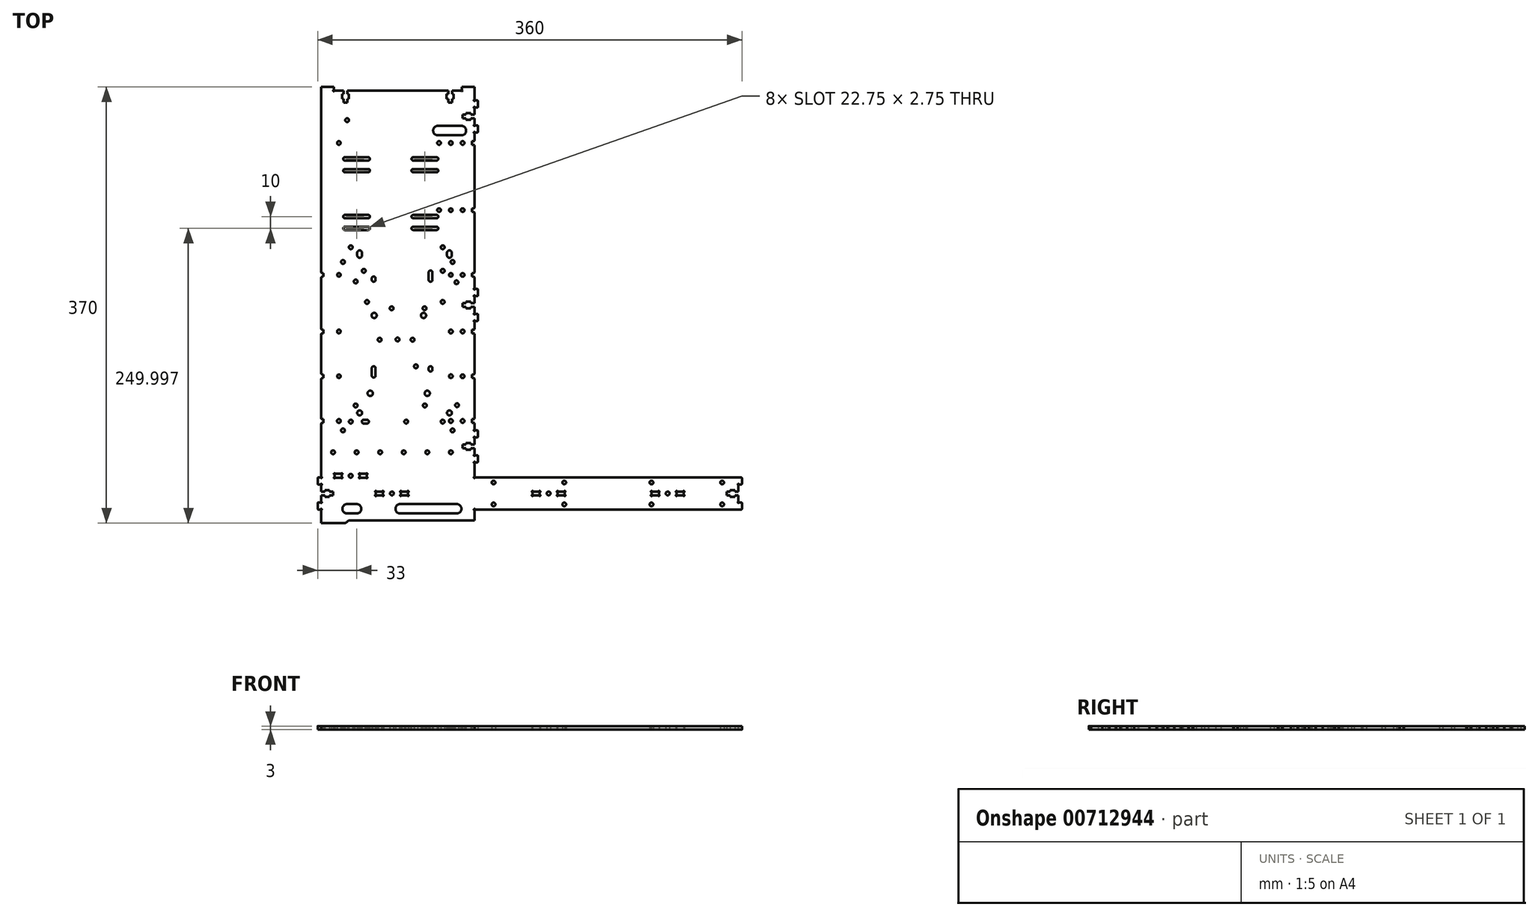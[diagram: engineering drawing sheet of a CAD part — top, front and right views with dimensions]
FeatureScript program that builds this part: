
annotation { "Feature Type Name" : "Feature", "Feature Type Description" : "" }
export const myFeature = defineFeature(function(context is Context, id is Id, definition is map)
    precondition{}
    {
        {
            var Q0;
            Q0=qCreatedBy(makeId("Top.planeOp"),FACE);
            var sketch = newSketch(context, id + "F0", { "sketchPlane" : qUnion([Q0])});
            skCircle(sketch, "E0", {"center": v(103.25, -146.86) * mm, "radius": 1.55 * mm});
            skCircle(sketch, "E1", {"center": v(-30.75, -146.86) * mm, "radius": 1.55 * mm});
            skCircle(sketch, "E2", {"center": v(163.25, -165.45) * mm, "radius": 1.55 * mm});
            skCircle(sketch, "E3", {"center": v(-30.75, -165.45) * mm, "radius": 1.55 * mm});
            skArc(sketch, "E4", {"start": v(104.17, -157.8) * mm, "mid": v(103.92, -157.87) * mm, "end": v(103.73, -158.05) * mm});
            skArc(sketch, "E5", {"start": v(103.05, -157.37) * mm, "mid": v(102.95, -158.16) * mm, "end": v(103.73, -158.05) * mm});
            skArc(sketch, "E6", {"start": v(103.05, -157.37) * mm, "mid": v(103.23, -157.19) * mm, "end": v(103.3, -156.94) * mm});
            skLineSegment(sketch, "E7", {"start": v(103.3, -155.37) * mm, "end": v(103.3, -156.94) * mm});
            skArc(sketch, "E8", {"start": v(103.3, -155.37) * mm, "mid": v(103.23, -155.12) * mm, "end": v(103.05, -154.94) * mm});
            skArc(sketch, "E9", {"start": v(103.73, -154.25) * mm, "mid": v(102.95, -154.15) * mm, "end": v(103.05, -154.94) * mm});
            skArc(sketch, "E10", {"start": v(103.73, -154.25) * mm, "mid": v(103.92, -154.44) * mm, "end": v(104.17, -154.5) * mm});
            skLineSegment(sketch, "E11", {"start": v(108.63, -154.5) * mm, "end": v(104.17, -154.5) * mm});
            skArc(sketch, "E12", {"start": v(108.63, -154.5) * mm, "mid": v(108.88, -154.44) * mm, "end": v(109.07, -154.25) * mm});
            skArc(sketch, "E13", {"start": v(109.75, -154.94) * mm, "mid": v(109.85, -154.15) * mm, "end": v(109.07, -154.25) * mm});
            skArc(sketch, "E14", {"start": v(109.75, -154.94) * mm, "mid": v(109.57, -155.12) * mm, "end": v(109.5, -155.37) * mm});
            skLineSegment(sketch, "E15", {"start": v(109.5, -156.94) * mm, "end": v(109.5, -155.37) * mm});
            skArc(sketch, "E16", {"start": v(109.5, -156.94) * mm, "mid": v(109.57, -157.19) * mm, "end": v(109.75, -157.37) * mm});
            skArc(sketch, "E17", {"start": v(109.07, -158.05) * mm, "mid": v(109.85, -158.16) * mm, "end": v(109.75, -157.37) * mm});
            skArc(sketch, "E18", {"start": v(109.07, -158.05) * mm, "mid": v(108.88, -157.87) * mm, "end": v(108.63, -157.8) * mm});
            skLineSegment(sketch, "E19", {"start": v(104.17, -157.8) * mm, "end": v(108.63, -157.8) * mm});
            skArc(sketch, "E20", {"start": v(125.37, -157.8) * mm, "mid": v(125.12, -157.87) * mm, "end": v(124.93, -158.05) * mm});
            skArc(sketch, "E21", {"start": v(124.25, -157.37) * mm, "mid": v(124.15, -158.16) * mm, "end": v(124.93, -158.05) * mm});
            skArc(sketch, "E22", {"start": v(124.25, -157.37) * mm, "mid": v(124.43, -157.19) * mm, "end": v(124.5, -156.94) * mm});
            skLineSegment(sketch, "E23", {"start": v(124.5, -155.37) * mm, "end": v(124.5, -156.94) * mm});
            skArc(sketch, "E24", {"start": v(124.5, -155.37) * mm, "mid": v(124.43, -155.12) * mm, "end": v(124.25, -154.94) * mm});
            skArc(sketch, "E25", {"start": v(124.93, -154.25) * mm, "mid": v(124.15, -154.15) * mm, "end": v(124.25, -154.94) * mm});
            skArc(sketch, "E26", {"start": v(124.93, -154.25) * mm, "mid": v(125.12, -154.44) * mm, "end": v(125.37, -154.5) * mm});
            skLineSegment(sketch, "E27", {"start": v(129.83, -154.5) * mm, "end": v(125.37, -154.5) * mm});
            skArc(sketch, "E28", {"start": v(129.83, -154.5) * mm, "mid": v(130.08, -154.44) * mm, "end": v(130.27, -154.25) * mm});
            skArc(sketch, "E29", {"start": v(130.95, -154.94) * mm, "mid": v(131.05, -154.15) * mm, "end": v(130.27, -154.25) * mm});
            skArc(sketch, "E30", {"start": v(130.95, -154.94) * mm, "mid": v(130.77, -155.12) * mm, "end": v(130.7, -155.37) * mm});
            skLineSegment(sketch, "E31", {"start": v(130.7, -156.94) * mm, "end": v(130.7, -155.37) * mm});
            skArc(sketch, "E32", {"start": v(130.7, -156.94) * mm, "mid": v(130.77, -157.19) * mm, "end": v(130.95, -157.37) * mm});
            skArc(sketch, "E33", {"start": v(130.27, -158.05) * mm, "mid": v(131.05, -158.16) * mm, "end": v(130.95, -157.37) * mm});
            skArc(sketch, "E34", {"start": v(130.27, -158.05) * mm, "mid": v(130.08, -157.87) * mm, "end": v(129.83, -157.8) * mm});
            skLineSegment(sketch, "E35", {"start": v(125.37, -157.8) * mm, "end": v(129.83, -157.8) * mm});
            skCircle(sketch, "E36", {"center": v(-67, 29.35) * mm, "radius": 1.55 * mm});
            skCircle(sketch, "E37", {"center": v(-77, 84.35) * mm, "radius": 1.55 * mm});
            skCircle(sketch, "E38", {"center": v(-73.88, 52.83) * mm, "radius": 1.6 * mm});
            skCircle(sketch, "E39", {"center": v(-151.88, -95.17) * mm, "radius": 1.6 * mm});
            skCircle(sketch, "E40", {"center": v(-90.17, -5.05) * mm, "radius": 2.23 * mm});
            skCircle(sketch, "E41", {"center": v(-87, -71.15) * mm, "radius": 2.23 * mm});
            skCircle(sketch, "E42", {"center": v(-87, -121.15) * mm, "radius": 1.6 * mm});
            skCircle(sketch, "E43", {"center": v(-127, -121.15) * mm, "radius": 1.6 * mm});
            skCircle(sketch, "E44", {"center": v(-167, -121.15) * mm, "radius": 1.6 * mm});
            skCircle(sketch, "E45", {"center": v(-162, -56.65) * mm, "radius": 1.55 * mm});
            skCircle(sketch, "E46", {"center": v(-162, 29.35) * mm, "radius": 1.55 * mm});
            skCircle(sketch, "E47", {"center": v(-140.88, 32.83) * mm, "radius": 1.6 * mm});
            skCircle(sketch, "E48", {"center": v(-73.88, 32.83) * mm, "radius": 1.6 * mm});
            skCircle(sketch, "E49", {"center": v(-65.5, 40.35) * mm, "radius": 1.6 * mm});
            skCircle(sketch, "E50", {"center": v(-65.5, -102.65) * mm, "radius": 1.6 * mm});
            skCircle(sketch, "E51", {"center": v(-112.23, -25.44) * mm, "radius": 1.6 * mm});
            skCircle(sketch, "E52", {"center": v(-61.73, -81.24) * mm, "radius": 1.6 * mm});
            skCircle(sketch, "E53", {"center": v(-147.73, 23.76) * mm, "radius": 1.6 * mm});
            skCircle(sketch, "E54", {"center": v(-62.23, 23.06) * mm, "radius": 1.6 * mm});
            skCircle(sketch, "E55", {"center": v(-73.88, 6.43) * mm, "radius": 1.6 * mm});
            skLineSegment(sketch, "E56", {"start": v(-134.07, 26.46) * mm, "end": v(-134.07, 25.19) * mm});
            skArc(sketch, "E57", {"start": v(-130.87, 26.46) * mm, "mid": v(-132.47, 28.06) * mm, "end": v(-134.07, 26.46) * mm});
            skLineSegment(sketch, "E58", {"start": v(-130.87, 25.19) * mm, "end": v(-130.87, 26.46) * mm});
            skArc(sketch, "E59", {"start": v(-134.07, 25.19) * mm, "mid": v(-132.47, 23.59) * mm, "end": v(-130.87, 25.19) * mm});
            skCircle(sketch, "E60", {"center": v(-127.39, -25.61) * mm, "radius": 1.6 * mm});
            skCircle(sketch, "E61", {"center": v(-99.45, -25.61) * mm, "radius": 1.6 * mm});
            skCircle(sketch, "E62", {"center": v(-57, 141.35) * mm, "radius": 1.55 * mm});
            skCircle(sketch, "E63", {"center": v(-67, -18.65) * mm, "radius": 1.6 * mm});
            skCircle(sketch, "E64", {"center": v(-67, -94.65) * mm, "radius": 1.6 * mm});
            skCircle(sketch, "E65", {"center": v(-57, -56.65) * mm, "radius": 1.55 * mm});
            skCircle(sketch, "E66", {"center": v(-57, -18.65) * mm, "radius": 1.55 * mm});
            skCircle(sketch, "E67", {"center": v(-152, -141.15) * mm, "radius": 1.6 * mm});
            skArc(sketch, "E68", {"start": v(-129.83, -157.8) * mm, "mid": v(-130.08, -157.87) * mm, "end": v(-130.27, -158.05) * mm});
            skArc(sketch, "E69", {"start": v(-130.95, -157.37) * mm, "mid": v(-131.05, -158.16) * mm, "end": v(-130.27, -158.05) * mm});
            skArc(sketch, "E70", {"start": v(-130.95, -157.37) * mm, "mid": v(-130.77, -157.19) * mm, "end": v(-130.7, -156.94) * mm});
            skLineSegment(sketch, "E71", {"start": v(-130.7, -155.37) * mm, "end": v(-130.7, -156.94) * mm});
            skArc(sketch, "E72", {"start": v(-130.7, -155.37) * mm, "mid": v(-130.77, -155.12) * mm, "end": v(-130.95, -154.94) * mm});
            skArc(sketch, "E73", {"start": v(-130.27, -154.25) * mm, "mid": v(-131.05, -154.15) * mm, "end": v(-130.95, -154.94) * mm});
            skArc(sketch, "E74", {"start": v(-130.27, -154.25) * mm, "mid": v(-130.08, -154.44) * mm, "end": v(-129.83, -154.5) * mm});
            skLineSegment(sketch, "E75", {"start": v(-125.37, -154.5) * mm, "end": v(-129.83, -154.5) * mm});
            skArc(sketch, "E76", {"start": v(-125.37, -154.5) * mm, "mid": v(-125.12, -154.44) * mm, "end": v(-124.93, -154.25) * mm});
            skArc(sketch, "E77", {"start": v(-124.25, -154.94) * mm, "mid": v(-124.15, -154.15) * mm, "end": v(-124.93, -154.25) * mm});
            skArc(sketch, "E78", {"start": v(-124.25, -154.94) * mm, "mid": v(-124.43, -155.12) * mm, "end": v(-124.5, -155.37) * mm});
            skLineSegment(sketch, "E79", {"start": v(-124.5, -156.94) * mm, "end": v(-124.5, -155.37) * mm});
            skArc(sketch, "E80", {"start": v(-124.5, -156.94) * mm, "mid": v(-124.43, -157.19) * mm, "end": v(-124.25, -157.37) * mm});
            skArc(sketch, "E81", {"start": v(-124.93, -158.05) * mm, "mid": v(-124.15, -158.16) * mm, "end": v(-124.25, -157.37) * mm});
            skArc(sketch, "E82", {"start": v(-124.93, -158.05) * mm, "mid": v(-125.12, -157.87) * mm, "end": v(-125.37, -157.8) * mm});
            skLineSegment(sketch, "E83", {"start": v(-129.83, -157.8) * mm, "end": v(-125.37, -157.8) * mm});
            skArc(sketch, "E84", {"start": v(-108.63, -157.8) * mm, "mid": v(-108.88, -157.87) * mm, "end": v(-109.07, -158.05) * mm});
            skArc(sketch, "E85", {"start": v(-109.75, -157.37) * mm, "mid": v(-109.85, -158.16) * mm, "end": v(-109.07, -158.05) * mm});
            skArc(sketch, "E86", {"start": v(-109.75, -157.37) * mm, "mid": v(-109.57, -157.19) * mm, "end": v(-109.5, -156.94) * mm});
            skLineSegment(sketch, "E87", {"start": v(-109.5, -155.37) * mm, "end": v(-109.5, -156.94) * mm});
            skArc(sketch, "E88", {"start": v(-109.5, -155.37) * mm, "mid": v(-109.57, -155.12) * mm, "end": v(-109.75, -154.94) * mm});
            skArc(sketch, "E89", {"start": v(-109.07, -154.25) * mm, "mid": v(-109.85, -154.15) * mm, "end": v(-109.75, -154.94) * mm});
            skArc(sketch, "E90", {"start": v(-109.07, -154.25) * mm, "mid": v(-108.88, -154.44) * mm, "end": v(-108.63, -154.5) * mm});
            skLineSegment(sketch, "E91", {"start": v(-104.17, -154.5) * mm, "end": v(-108.63, -154.5) * mm});
            skArc(sketch, "E92", {"start": v(-104.17, -154.5) * mm, "mid": v(-103.92, -154.44) * mm, "end": v(-103.73, -154.25) * mm});
            skArc(sketch, "E93", {"start": v(-103.05, -154.94) * mm, "mid": v(-102.95, -154.15) * mm, "end": v(-103.73, -154.25) * mm});
            skArc(sketch, "E94", {"start": v(-103.05, -154.94) * mm, "mid": v(-103.23, -155.12) * mm, "end": v(-103.3, -155.37) * mm});
            skLineSegment(sketch, "E95", {"start": v(-103.3, -156.94) * mm, "end": v(-103.3, -155.37) * mm});
            skArc(sketch, "E96", {"start": v(-103.3, -156.94) * mm, "mid": v(-103.23, -157.19) * mm, "end": v(-103.05, -157.37) * mm});
            skArc(sketch, "E97", {"start": v(-103.73, -158.05) * mm, "mid": v(-102.95, -158.16) * mm, "end": v(-103.05, -157.37) * mm});
            skArc(sketch, "E98", {"start": v(-103.73, -158.05) * mm, "mid": v(-103.92, -157.87) * mm, "end": v(-104.17, -157.8) * mm});
            skLineSegment(sketch, "E99", {"start": v(-108.63, -157.8) * mm, "end": v(-104.17, -157.8) * mm});
            skLineSegment(sketch, "E100", {"start": v(-155, -173.15) * mm, "end": v(-147, -173.15) * mm});
            skArc(sketch, "E101", {"start": v(-155, -165.15) * mm, "mid": v(-159, -169.15) * mm, "end": v(-155, -173.15) * mm});
            skLineSegment(sketch, "E102", {"start": v(-147, -165.15) * mm, "end": v(-155, -165.15) * mm});
            skArc(sketch, "E103", {"start": v(-147, -173.15) * mm, "mid": v(-143, -169.15) * mm, "end": v(-147, -165.15) * mm});
            skCircle(sketch, "E104", {"center": v(-155, 160.75) * mm, "radius": 1.6 * mm});
            skCircle(sketch, "E105", {"center": v(16, -156.15) * mm, "radius": 1.6 * mm});
            skArc(sketch, "E106", {"start": v(-47, -170.62) * mm, "mid": v(-47.07, -170.37) * mm, "end": v(-47.25, -170.19) * mm});
            skArc(sketch, "E107", {"start": v(-46.57, -169.5) * mm, "mid": v(-47.35, -169.4) * mm, "end": v(-47.25, -170.19) * mm});
            skArc(sketch, "E108", {"start": v(-46.57, -169.5) * mm, "mid": v(-46.38, -169.69) * mm, "end": v(-46.13, -169.75) * mm});
            skLineSegment(sketch, "E109", {"start": v(-46.13, -169.75) * mm, "end": v(179.5, -169.75) * mm});
            skArc(sketch, "E110", {"start": v(179.5, -169.75) * mm, "mid": v(179.85, -169.6) * mm, "end": v(180, -169.25) * mm});
            skLineSegment(sketch, "E111", {"start": v(180, -169.25) * mm, "end": v(180, -164.25) * mm});
            skArc(sketch, "E112", {"start": v(180, -164.25) * mm, "mid": v(179.85, -163.9) * mm, "end": v(179.5, -163.75) * mm});
            skLineSegment(sketch, "E113", {"start": v(179.5, -163.75) * mm, "end": v(177.87, -163.75) * mm});
            skArc(sketch, "E114", {"start": v(177.87, -163.75) * mm, "mid": v(177.62, -163.82) * mm, "end": v(177.43, -164) * mm});
            skArc(sketch, "E115", {"start": v(176.75, -163.32) * mm, "mid": v(176.65, -164.1) * mm, "end": v(177.43, -164) * mm});
            skArc(sketch, "E116", {"start": v(176.75, -163.32) * mm, "mid": v(176.93, -163.14) * mm, "end": v(177, -162.89) * mm});
            skLineSegment(sketch, "E117", {"start": v(177, -162.89) * mm, "end": v(177, -157.75) * mm});
            skLineSegment(sketch, "E118", {"start": v(177, -157.75) * mm, "end": v(174, -157.75) * mm});
            skLineSegment(sketch, "E119", {"start": v(174, -157.75) * mm, "end": v(174, -159.03) * mm});
            skLineSegment(sketch, "E120", {"start": v(174, -159.03) * mm, "end": v(170, -159.03) * mm});
            skLineSegment(sketch, "E121", {"start": v(170, -159.03) * mm, "end": v(170, -157.75) * mm});
            skLineSegment(sketch, "E122", {"start": v(170, -157.75) * mm, "end": v(167, -157.75) * mm});
            skLineSegment(sketch, "E123", {"start": v(167, -157.75) * mm, "end": v(167, -154.55) * mm});
            skLineSegment(sketch, "E124", {"start": v(167, -154.55) * mm, "end": v(170, -154.55) * mm});
            skLineSegment(sketch, "E125", {"start": v(170, -154.55) * mm, "end": v(170, -153.28) * mm});
            skLineSegment(sketch, "E126", {"start": v(170, -153.28) * mm, "end": v(174, -153.28) * mm});
            skLineSegment(sketch, "E127", {"start": v(174, -153.28) * mm, "end": v(174, -154.55) * mm});
            skLineSegment(sketch, "E128", {"start": v(174, -154.55) * mm, "end": v(177, -154.55) * mm});
            skLineSegment(sketch, "E129", {"start": v(177, -154.55) * mm, "end": v(177, -149.42) * mm});
            skArc(sketch, "E130", {"start": v(177, -149.42) * mm, "mid": v(176.93, -149.17) * mm, "end": v(176.75, -148.99) * mm});
            skArc(sketch, "E131", {"start": v(177.43, -148.3) * mm, "mid": v(176.65, -148.2) * mm, "end": v(176.75, -148.99) * mm});
            skArc(sketch, "E132", {"start": v(177.43, -148.3) * mm, "mid": v(177.62, -148.49) * mm, "end": v(177.87, -148.55) * mm});
            skLineSegment(sketch, "E133", {"start": v(177.87, -148.55) * mm, "end": v(179.5, -148.55) * mm});
            skArc(sketch, "E134", {"start": v(179.5, -148.55) * mm, "mid": v(179.85, -148.4) * mm, "end": v(180, -148.05) * mm});
            skLineSegment(sketch, "E135", {"start": v(180, -148.05) * mm, "end": v(180, -143.05) * mm});
            skArc(sketch, "E136", {"start": v(180, -143.05) * mm, "mid": v(179.85, -142.7) * mm, "end": v(179.5, -142.55) * mm});
            skLineSegment(sketch, "E137", {"start": v(179.5, -142.55) * mm, "end": v(-46.13, -142.55) * mm});
            skArc(sketch, "E138", {"start": v(-46.13, -142.55) * mm, "mid": v(-46.38, -142.62) * mm, "end": v(-46.57, -142.8) * mm});
            skArc(sketch, "E139", {"start": v(-47.25, -142.12) * mm, "mid": v(-47.35, -142.9) * mm, "end": v(-46.57, -142.8) * mm});
            skArc(sketch, "E140", {"start": v(-47.25, -142.12) * mm, "mid": v(-47.07, -141.94) * mm, "end": v(-47, -141.69) * mm});
            skLineSegment(sketch, "E141", {"start": v(-47, -141.69) * mm, "end": v(-47, -130.62) * mm});
            skArc(sketch, "E142", {"start": v(-47, -130.62) * mm, "mid": v(-47.07, -130.37) * mm, "end": v(-47.25, -130.19) * mm});
            skArc(sketch, "E143", {"start": v(-46.57, -129.5) * mm, "mid": v(-47.35, -129.4) * mm, "end": v(-47.25, -130.19) * mm});
            skArc(sketch, "E144", {"start": v(-46.57, -129.5) * mm, "mid": v(-46.38, -129.69) * mm, "end": v(-46.13, -129.75) * mm});
            skLineSegment(sketch, "E145", {"start": v(-46.13, -129.75) * mm, "end": v(-44.5, -129.75) * mm});
            skArc(sketch, "E146", {"start": v(-44.5, -129.75) * mm, "mid": v(-44.15, -129.6) * mm, "end": v(-44, -129.25) * mm});
            skLineSegment(sketch, "E147", {"start": v(-44, -129.25) * mm, "end": v(-44, -124.25) * mm});
            skArc(sketch, "E148", {"start": v(-44, -124.25) * mm, "mid": v(-44.15, -123.9) * mm, "end": v(-44.5, -123.75) * mm});
            skLineSegment(sketch, "E149", {"start": v(-44.5, -123.75) * mm, "end": v(-46.13, -123.75) * mm});
            skArc(sketch, "E150", {"start": v(-46.13, -123.75) * mm, "mid": v(-46.38, -123.82) * mm, "end": v(-46.57, -124) * mm});
            skArc(sketch, "E151", {"start": v(-47.25, -123.32) * mm, "mid": v(-47.35, -124.1) * mm, "end": v(-46.57, -124) * mm});
            skArc(sketch, "E152", {"start": v(-47.25, -123.32) * mm, "mid": v(-47.07, -123.14) * mm, "end": v(-47, -122.89) * mm});
            skLineSegment(sketch, "E153", {"start": v(-47, -122.89) * mm, "end": v(-47, -117.75) * mm});
            skLineSegment(sketch, "E154", {"start": v(-47, -117.75) * mm, "end": v(-50, -117.75) * mm});
            skLineSegment(sketch, "E155", {"start": v(-50, -117.75) * mm, "end": v(-50, -119.03) * mm});
            skLineSegment(sketch, "E156", {"start": v(-50, -119.03) * mm, "end": v(-54, -119.03) * mm});
            skLineSegment(sketch, "E157", {"start": v(-54, -119.03) * mm, "end": v(-54, -117.75) * mm});
            skLineSegment(sketch, "E158", {"start": v(-54, -117.75) * mm, "end": v(-57, -117.75) * mm});
            skLineSegment(sketch, "E159", {"start": v(-57, -117.75) * mm, "end": v(-57, -114.55) * mm});
            skLineSegment(sketch, "E160", {"start": v(-57, -114.55) * mm, "end": v(-54, -114.55) * mm});
            skLineSegment(sketch, "E161", {"start": v(-54, -114.55) * mm, "end": v(-54, -113.28) * mm});
            skLineSegment(sketch, "E162", {"start": v(-54, -113.28) * mm, "end": v(-50, -113.28) * mm});
            skLineSegment(sketch, "E163", {"start": v(-50, -113.28) * mm, "end": v(-50, -114.55) * mm});
            skLineSegment(sketch, "E164", {"start": v(-50, -114.55) * mm, "end": v(-47, -114.55) * mm});
            skLineSegment(sketch, "E165", {"start": v(-47, -114.55) * mm, "end": v(-47, -109.42) * mm});
            skArc(sketch, "E166", {"start": v(-47, -109.42) * mm, "mid": v(-47.07, -109.17) * mm, "end": v(-47.25, -108.99) * mm});
            skArc(sketch, "E167", {"start": v(-46.57, -108.3) * mm, "mid": v(-47.35, -108.2) * mm, "end": v(-47.25, -108.99) * mm});
            skArc(sketch, "E168", {"start": v(-46.57, -108.3) * mm, "mid": v(-46.38, -108.49) * mm, "end": v(-46.13, -108.55) * mm});
            skLineSegment(sketch, "E169", {"start": v(-46.13, -108.55) * mm, "end": v(-44.5, -108.55) * mm});
            skArc(sketch, "E170", {"start": v(-44.5, -108.55) * mm, "mid": v(-44.15, -108.4) * mm, "end": v(-44, -108.05) * mm});
            skLineSegment(sketch, "E171", {"start": v(-44, -108.05) * mm, "end": v(-44, -103.05) * mm});
            skArc(sketch, "E172", {"start": v(-44, -103.05) * mm, "mid": v(-44.15, -102.7) * mm, "end": v(-44.5, -102.55) * mm});
            skLineSegment(sketch, "E173", {"start": v(-44.5, -102.55) * mm, "end": v(-46.13, -102.55) * mm});
            skArc(sketch, "E174", {"start": v(-46.13, -102.55) * mm, "mid": v(-46.38, -102.62) * mm, "end": v(-46.57, -102.8) * mm});
            skArc(sketch, "E175", {"start": v(-47.25, -102.12) * mm, "mid": v(-47.35, -102.9) * mm, "end": v(-46.57, -102.8) * mm});
            skArc(sketch, "E176", {"start": v(-47.25, -102.12) * mm, "mid": v(-47.07, -101.94) * mm, "end": v(-47, -101.69) * mm});
            skLineSegment(sketch, "E177", {"start": v(-47, -101.69) * mm, "end": v(-47, -96.65) * mm});
            skLineSegment(sketch, "E178", {"start": v(-47, -96.65) * mm, "end": v(-47.5, -96.15) * mm});
            skLineSegment(sketch, "E179", {"start": v(-47.5, -96.15) * mm, "end": v(-49, -96.15) * mm});
            skLineSegment(sketch, "E180", {"start": v(-49, -96.15) * mm, "end": v(-49, -93.15) * mm});
            skLineSegment(sketch, "E181", {"start": v(-49, -93.15) * mm, "end": v(-47.5, -93.15) * mm});
            skLineSegment(sketch, "E182", {"start": v(-47.5, -93.15) * mm, "end": v(-47, -92.65) * mm});
            skLineSegment(sketch, "E183", {"start": v(-47, -92.65) * mm, "end": v(-47, -58.65) * mm});
            skLineSegment(sketch, "E184", {"start": v(-47, -58.65) * mm, "end": v(-47.5, -58.15) * mm});
            skLineSegment(sketch, "E185", {"start": v(-47.5, -58.15) * mm, "end": v(-49, -58.15) * mm});
            skLineSegment(sketch, "E186", {"start": v(-49, -58.15) * mm, "end": v(-49, -55.15) * mm});
            skLineSegment(sketch, "E187", {"start": v(-49, -55.15) * mm, "end": v(-47.5, -55.15) * mm});
            skLineSegment(sketch, "E188", {"start": v(-47.5, -55.15) * mm, "end": v(-47, -54.65) * mm});
            skLineSegment(sketch, "E189", {"start": v(-47, -54.65) * mm, "end": v(-47, -20.65) * mm});
            skLineSegment(sketch, "E190", {"start": v(-47, -20.65) * mm, "end": v(-47.5, -20.15) * mm});
            skLineSegment(sketch, "E191", {"start": v(-47.5, -20.15) * mm, "end": v(-49, -20.15) * mm});
            skLineSegment(sketch, "E192", {"start": v(-49, -20.15) * mm, "end": v(-49, -17.15) * mm});
            skLineSegment(sketch, "E193", {"start": v(-49, -17.15) * mm, "end": v(-47.5, -17.15) * mm});
            skLineSegment(sketch, "E194", {"start": v(-47.5, -17.15) * mm, "end": v(-47, -16.65) * mm});
            skLineSegment(sketch, "E195", {"start": v(-47, -16.65) * mm, "end": v(-47, -10.62) * mm});
            skArc(sketch, "E196", {"start": v(-47, -10.62) * mm, "mid": v(-47.07, -10.37) * mm, "end": v(-47.25, -10.19) * mm});
            skArc(sketch, "E197", {"start": v(-46.57, -9.5) * mm, "mid": v(-47.35, -9.4) * mm, "end": v(-47.25, -10.19) * mm});
            skArc(sketch, "E198", {"start": v(-46.57, -9.5) * mm, "mid": v(-46.38, -9.69) * mm, "end": v(-46.13, -9.75) * mm});
            skLineSegment(sketch, "E199", {"start": v(-46.13, -9.75) * mm, "end": v(-44.5, -9.75) * mm});
            skArc(sketch, "E200", {"start": v(-44.5, -9.75) * mm, "mid": v(-44.15, -9.6) * mm, "end": v(-44, -9.25) * mm});
            skLineSegment(sketch, "E201", {"start": v(-44, -9.25) * mm, "end": v(-44, -4.25) * mm});
            skArc(sketch, "E202", {"start": v(-44, -4.25) * mm, "mid": v(-44.15, -3.9) * mm, "end": v(-44.5, -3.75) * mm});
            skLineSegment(sketch, "E203", {"start": v(-44.5, -3.75) * mm, "end": v(-46.13, -3.75) * mm});
            skArc(sketch, "E204", {"start": v(-46.13, -3.75) * mm, "mid": v(-46.38, -3.82) * mm, "end": v(-46.57, -4) * mm});
            skArc(sketch, "E205", {"start": v(-47.25, -3.32) * mm, "mid": v(-47.35, -4.1) * mm, "end": v(-46.57, -4) * mm});
            skArc(sketch, "E206", {"start": v(-47.25, -3.32) * mm, "mid": v(-47.07, -3.14) * mm, "end": v(-47, -2.89) * mm});
            skLineSegment(sketch, "E207", {"start": v(-47, -2.89) * mm, "end": v(-47, 2.25) * mm});
            skLineSegment(sketch, "E208", {"start": v(-47, 2.25) * mm, "end": v(-50, 2.25) * mm});
            skLineSegment(sketch, "E209", {"start": v(-50, 2.25) * mm, "end": v(-50, 0.97) * mm});
            skLineSegment(sketch, "E210", {"start": v(-50, 0.97) * mm, "end": v(-54, 0.97) * mm});
            skLineSegment(sketch, "E211", {"start": v(-54, 0.97) * mm, "end": v(-54, 2.25) * mm});
            skLineSegment(sketch, "E212", {"start": v(-54, 2.25) * mm, "end": v(-57, 2.25) * mm});
            skLineSegment(sketch, "E213", {"start": v(-57, 2.25) * mm, "end": v(-57, 5.45) * mm});
            skLineSegment(sketch, "E214", {"start": v(-57, 5.45) * mm, "end": v(-54, 5.45) * mm});
            skLineSegment(sketch, "E215", {"start": v(-54, 5.45) * mm, "end": v(-54, 6.72) * mm});
            skLineSegment(sketch, "E216", {"start": v(-54, 6.72) * mm, "end": v(-50, 6.72) * mm});
            skLineSegment(sketch, "E217", {"start": v(-50, 6.72) * mm, "end": v(-50, 5.45) * mm});
            skLineSegment(sketch, "E218", {"start": v(-50, 5.45) * mm, "end": v(-47, 5.45) * mm});
            skLineSegment(sketch, "E219", {"start": v(-47, 5.45) * mm, "end": v(-47, 10.58) * mm});
            skArc(sketch, "E220", {"start": v(-47, 10.58) * mm, "mid": v(-47.07, 10.83) * mm, "end": v(-47.25, 11.01) * mm});
            skArc(sketch, "E221", {"start": v(-46.57, 11.7) * mm, "mid": v(-47.35, 11.8) * mm, "end": v(-47.25, 11.01) * mm});
            skArc(sketch, "E222", {"start": v(-46.57, 11.7) * mm, "mid": v(-46.38, 11.51) * mm, "end": v(-46.13, 11.45) * mm});
            skLineSegment(sketch, "E223", {"start": v(-46.13, 11.45) * mm, "end": v(-44.5, 11.45) * mm});
            skArc(sketch, "E224", {"start": v(-44.5, 11.45) * mm, "mid": v(-44.15, 11.6) * mm, "end": v(-44, 11.95) * mm});
            skLineSegment(sketch, "E225", {"start": v(-44, 11.95) * mm, "end": v(-44, 16.95) * mm});
            skArc(sketch, "E226", {"start": v(-44, 16.95) * mm, "mid": v(-44.15, 17.3) * mm, "end": v(-44.5, 17.45) * mm});
            skLineSegment(sketch, "E227", {"start": v(-44.5, 17.45) * mm, "end": v(-46.13, 17.45) * mm});
            skArc(sketch, "E228", {"start": v(-46.13, 17.45) * mm, "mid": v(-46.38, 17.38) * mm, "end": v(-46.57, 17.2) * mm});
            skArc(sketch, "E229", {"start": v(-47.25, 17.88) * mm, "mid": v(-47.35, 17.1) * mm, "end": v(-46.57, 17.2) * mm});
            skArc(sketch, "E230", {"start": v(-47.25, 17.88) * mm, "mid": v(-47.07, 18.06) * mm, "end": v(-47, 18.31) * mm});
            skLineSegment(sketch, "E231", {"start": v(-47, 18.31) * mm, "end": v(-47, 27.35) * mm});
            skLineSegment(sketch, "E232", {"start": v(-47, 27.35) * mm, "end": v(-47.5, 27.85) * mm});
            skLineSegment(sketch, "E233", {"start": v(-47.5, 27.85) * mm, "end": v(-49, 27.85) * mm});
            skLineSegment(sketch, "E234", {"start": v(-49, 27.85) * mm, "end": v(-49, 30.85) * mm});
            skLineSegment(sketch, "E235", {"start": v(-49, 30.85) * mm, "end": v(-47.5, 30.85) * mm});
            skLineSegment(sketch, "E236", {"start": v(-47.5, 30.85) * mm, "end": v(-47, 31.35) * mm});
            skLineSegment(sketch, "E237", {"start": v(-47, 31.35) * mm, "end": v(-47, 82.35) * mm});
            skLineSegment(sketch, "E238", {"start": v(-47, 82.35) * mm, "end": v(-47.5, 82.85) * mm});
            skLineSegment(sketch, "E239", {"start": v(-47.5, 82.85) * mm, "end": v(-49, 82.85) * mm});
            skLineSegment(sketch, "E240", {"start": v(-49, 82.85) * mm, "end": v(-49, 85.85) * mm});
            skLineSegment(sketch, "E241", {"start": v(-49, 85.85) * mm, "end": v(-47.5, 85.85) * mm});
            skLineSegment(sketch, "E242", {"start": v(-47.5, 85.85) * mm, "end": v(-47, 86.35) * mm});
            skLineSegment(sketch, "E243", {"start": v(-47, 86.35) * mm, "end": v(-47, 139.35) * mm});
            skLineSegment(sketch, "E244", {"start": v(-47, 139.35) * mm, "end": v(-47.5, 139.85) * mm});
            skLineSegment(sketch, "E245", {"start": v(-47.5, 139.85) * mm, "end": v(-49, 139.85) * mm});
            skLineSegment(sketch, "E246", {"start": v(-49, 139.85) * mm, "end": v(-49, 142.85) * mm});
            skLineSegment(sketch, "E247", {"start": v(-49, 142.85) * mm, "end": v(-47.5, 142.85) * mm});
            skLineSegment(sketch, "E248", {"start": v(-47.5, 142.85) * mm, "end": v(-47, 143.35) * mm});
            skLineSegment(sketch, "E249", {"start": v(-47, 143.35) * mm, "end": v(-47, 149.38) * mm});
            skArc(sketch, "E250", {"start": v(-47, 149.38) * mm, "mid": v(-47.07, 149.63) * mm, "end": v(-47.25, 149.81) * mm});
            skArc(sketch, "E251", {"start": v(-46.57, 150.5) * mm, "mid": v(-47.35, 150.6) * mm, "end": v(-47.25, 149.81) * mm});
            skArc(sketch, "E252", {"start": v(-46.57, 150.5) * mm, "mid": v(-46.38, 150.31) * mm, "end": v(-46.13, 150.25) * mm});
            skLineSegment(sketch, "E253", {"start": v(-46.13, 150.25) * mm, "end": v(-44.5, 150.25) * mm});
            skArc(sketch, "E254", {"start": v(-44.5, 150.25) * mm, "mid": v(-44.15, 150.4) * mm, "end": v(-44, 150.75) * mm});
            skLineSegment(sketch, "E255", {"start": v(-44, 150.75) * mm, "end": v(-44, 155.75) * mm});
            skArc(sketch, "E256", {"start": v(-44, 155.75) * mm, "mid": v(-44.15, 156.1) * mm, "end": v(-44.5, 156.25) * mm});
            skLineSegment(sketch, "E257", {"start": v(-44.5, 156.25) * mm, "end": v(-46.13, 156.25) * mm});
            skArc(sketch, "E258", {"start": v(-46.13, 156.25) * mm, "mid": v(-46.38, 156.18) * mm, "end": v(-46.57, 156) * mm});
            skArc(sketch, "E259", {"start": v(-47.25, 156.68) * mm, "mid": v(-47.35, 155.9) * mm, "end": v(-46.57, 156) * mm});
            skArc(sketch, "E260", {"start": v(-47.25, 156.68) * mm, "mid": v(-47.07, 156.86) * mm, "end": v(-47, 157.11) * mm});
            skLineSegment(sketch, "E261", {"start": v(-47, 157.11) * mm, "end": v(-47, 162.25) * mm});
            skLineSegment(sketch, "E262", {"start": v(-47, 162.25) * mm, "end": v(-50, 162.25) * mm});
            skLineSegment(sketch, "E263", {"start": v(-50, 162.25) * mm, "end": v(-50, 160.97) * mm});
            skLineSegment(sketch, "E264", {"start": v(-50, 160.97) * mm, "end": v(-54, 160.97) * mm});
            skLineSegment(sketch, "E265", {"start": v(-54, 160.97) * mm, "end": v(-54, 162.25) * mm});
            skLineSegment(sketch, "E266", {"start": v(-54, 162.25) * mm, "end": v(-57, 162.25) * mm});
            skLineSegment(sketch, "E267", {"start": v(-57, 162.25) * mm, "end": v(-57, 165.45) * mm});
            skLineSegment(sketch, "E268", {"start": v(-57, 165.45) * mm, "end": v(-54, 165.45) * mm});
            skLineSegment(sketch, "E269", {"start": v(-54, 165.45) * mm, "end": v(-54, 166.72) * mm});
            skLineSegment(sketch, "E270", {"start": v(-54, 166.72) * mm, "end": v(-50, 166.72) * mm});
            skLineSegment(sketch, "E271", {"start": v(-50, 166.72) * mm, "end": v(-50, 165.45) * mm});
            skLineSegment(sketch, "E272", {"start": v(-50, 165.45) * mm, "end": v(-47, 165.45) * mm});
            skLineSegment(sketch, "E273", {"start": v(-47, 165.45) * mm, "end": v(-47, 170.58) * mm});
            skArc(sketch, "E274", {"start": v(-47, 170.58) * mm, "mid": v(-47.07, 170.83) * mm, "end": v(-47.25, 171.01) * mm});
            skArc(sketch, "E275", {"start": v(-46.57, 171.7) * mm, "mid": v(-47.35, 171.8) * mm, "end": v(-47.25, 171.01) * mm});
            skArc(sketch, "E276", {"start": v(-46.57, 171.7) * mm, "mid": v(-46.38, 171.51) * mm, "end": v(-46.13, 171.45) * mm});
            skLineSegment(sketch, "E277", {"start": v(-46.13, 171.45) * mm, "end": v(-44.5, 171.45) * mm});
            skArc(sketch, "E278", {"start": v(-44.5, 171.45) * mm, "mid": v(-44.15, 171.6) * mm, "end": v(-44, 171.95) * mm});
            skLineSegment(sketch, "E279", {"start": v(-44, 171.95) * mm, "end": v(-44, 176.95) * mm});
            skArc(sketch, "E280", {"start": v(-44, 176.95) * mm, "mid": v(-44.15, 177.3) * mm, "end": v(-44.5, 177.45) * mm});
            skLineSegment(sketch, "E281", {"start": v(-44.5, 177.45) * mm, "end": v(-46.13, 177.45) * mm});
            skArc(sketch, "E282", {"start": v(-46.13, 177.45) * mm, "mid": v(-46.38, 177.38) * mm, "end": v(-46.57, 177.2) * mm});
            skArc(sketch, "E283", {"start": v(-47.25, 177.88) * mm, "mid": v(-47.35, 177.1) * mm, "end": v(-46.57, 177.2) * mm});
            skArc(sketch, "E284", {"start": v(-47.25, 177.88) * mm, "mid": v(-47.07, 178.06) * mm, "end": v(-47, 178.31) * mm});
            skLineSegment(sketch, "E285", {"start": v(-47, 178.31) * mm, "end": v(-47, 188.85) * mm});
            skLineSegment(sketch, "E286", {"start": v(-47, 188.85) * mm, "end": v(-57.65, 188.85) * mm});
            skLineSegment(sketch, "E287", {"start": v(-57.65, 188.85) * mm, "end": v(-57.65, 186.61) * mm});
            skArc(sketch, "E288", {"start": v(-57.65, 186.61) * mm, "mid": v(-57.58, 186.36) * mm, "end": v(-57.4, 186.18) * mm});
            skArc(sketch, "E289", {"start": v(-58.08, 185.5) * mm, "mid": v(-57.3, 185.4) * mm, "end": v(-57.4, 186.18) * mm});
            skArc(sketch, "E290", {"start": v(-58.08, 185.5) * mm, "mid": v(-58.27, 185.68) * mm, "end": v(-58.52, 185.75) * mm});
            skLineSegment(sketch, "E291", {"start": v(-58.52, 185.75) * mm, "end": v(-66.05, 185.75) * mm});
            skLineSegment(sketch, "E292", {"start": v(-66.05, 185.75) * mm, "end": v(-66.05, 182.75) * mm});
            skLineSegment(sketch, "E293", {"start": v(-66.05, 182.75) * mm, "end": v(-64.78, 182.75) * mm});
            skLineSegment(sketch, "E294", {"start": v(-64.78, 182.75) * mm, "end": v(-64.78, 178.75) * mm});
            skLineSegment(sketch, "E295", {"start": v(-64.78, 178.75) * mm, "end": v(-66.05, 178.75) * mm});
            skLineSegment(sketch, "E296", {"start": v(-66.05, 178.75) * mm, "end": v(-66.05, 175.75) * mm});
            skLineSegment(sketch, "E297", {"start": v(-66.05, 175.75) * mm, "end": v(-69.25, 175.75) * mm});
            skLineSegment(sketch, "E298", {"start": v(-69.25, 175.75) * mm, "end": v(-69.25, 178.75) * mm});
            skLineSegment(sketch, "E299", {"start": v(-69.25, 178.75) * mm, "end": v(-70.53, 178.75) * mm});
            skLineSegment(sketch, "E300", {"start": v(-70.53, 178.75) * mm, "end": v(-70.53, 182.75) * mm});
            skLineSegment(sketch, "E301", {"start": v(-70.53, 182.75) * mm, "end": v(-69.25, 182.75) * mm});
            skLineSegment(sketch, "E302", {"start": v(-69.25, 182.75) * mm, "end": v(-69.25, 185.75) * mm});
            skLineSegment(sketch, "E303", {"start": v(-69.25, 185.75) * mm, "end": v(-154.75, 185.75) * mm});
            skLineSegment(sketch, "E304", {"start": v(-154.75, 185.75) * mm, "end": v(-154.75, 182.75) * mm});
            skLineSegment(sketch, "E305", {"start": v(-154.75, 182.75) * mm, "end": v(-153.47, 182.75) * mm});
            skLineSegment(sketch, "E306", {"start": v(-153.47, 182.75) * mm, "end": v(-153.47, 178.75) * mm});
            skLineSegment(sketch, "E307", {"start": v(-153.47, 178.75) * mm, "end": v(-154.75, 178.75) * mm});
            skLineSegment(sketch, "E308", {"start": v(-154.75, 178.75) * mm, "end": v(-154.75, 175.75) * mm});
            skLineSegment(sketch, "E309", {"start": v(-154.75, 175.75) * mm, "end": v(-157.95, 175.75) * mm});
            skLineSegment(sketch, "E310", {"start": v(-157.95, 175.75) * mm, "end": v(-157.95, 178.75) * mm});
            skLineSegment(sketch, "E311", {"start": v(-157.95, 178.75) * mm, "end": v(-159.22, 178.75) * mm});
            skLineSegment(sketch, "E312", {"start": v(-159.22, 178.75) * mm, "end": v(-159.22, 182.75) * mm});
            skLineSegment(sketch, "E313", {"start": v(-159.22, 182.75) * mm, "end": v(-157.95, 182.75) * mm});
            skLineSegment(sketch, "E314", {"start": v(-157.95, 182.75) * mm, "end": v(-157.95, 185.75) * mm});
            skLineSegment(sketch, "E315", {"start": v(-157.95, 185.75) * mm, "end": v(-165.48, 185.75) * mm});
            skArc(sketch, "E316", {"start": v(-165.48, 185.75) * mm, "mid": v(-165.73, 185.68) * mm, "end": v(-165.92, 185.5) * mm});
            skArc(sketch, "E317", {"start": v(-166.6, 186.18) * mm, "mid": v(-166.7, 185.4) * mm, "end": v(-165.92, 185.5) * mm});
            skArc(sketch, "E318", {"start": v(-166.6, 186.18) * mm, "mid": v(-166.42, 186.36) * mm, "end": v(-166.35, 186.61) * mm});
            skLineSegment(sketch, "E319", {"start": v(-166.35, 186.61) * mm, "end": v(-166.35, 188.85) * mm});
            skLineSegment(sketch, "E320", {"start": v(-166.35, 188.85) * mm, "end": v(-177, 188.85) * mm});
            skLineSegment(sketch, "E321", {"start": v(-177, 188.85) * mm, "end": v(-177, 31.85) * mm});
            skArc(sketch, "E322", {"start": v(-177, 31.85) * mm, "mid": v(-176.7, 31.14) * mm, "end": v(-176, 30.85) * mm});
            skLineSegment(sketch, "E323", {"start": v(-176, 30.85) * mm, "end": v(-175, 30.85) * mm});
            skLineSegment(sketch, "E324", {"start": v(-175, 30.85) * mm, "end": v(-175, 27.85) * mm});
            skLineSegment(sketch, "E325", {"start": v(-175, 27.85) * mm, "end": v(-176, 27.85) * mm});
            skArc(sketch, "E326", {"start": v(-176, 27.85) * mm, "mid": v(-176.7, 27.55) * mm, "end": v(-177, 26.85) * mm});
            skLineSegment(sketch, "E327", {"start": v(-177, 26.85) * mm, "end": v(-177, -16.15) * mm});
            skArc(sketch, "E328", {"start": v(-177, -16.15) * mm, "mid": v(-176.7, -16.86) * mm, "end": v(-176, -17.15) * mm});
            skLineSegment(sketch, "E329", {"start": v(-176, -17.15) * mm, "end": v(-175, -17.15) * mm});
            skLineSegment(sketch, "E330", {"start": v(-175, -17.15) * mm, "end": v(-175, -20.15) * mm});
            skLineSegment(sketch, "E331", {"start": v(-175, -20.15) * mm, "end": v(-176, -20.15) * mm});
            skArc(sketch, "E332", {"start": v(-176, -20.15) * mm, "mid": v(-176.7, -20.45) * mm, "end": v(-177, -21.15) * mm});
            skLineSegment(sketch, "E333", {"start": v(-177, -21.15) * mm, "end": v(-177, -54.15) * mm});
            skArc(sketch, "E334", {"start": v(-177, -54.15) * mm, "mid": v(-176.7, -54.86) * mm, "end": v(-176, -55.15) * mm});
            skLineSegment(sketch, "E335", {"start": v(-176, -55.15) * mm, "end": v(-175, -55.15) * mm});
            skLineSegment(sketch, "E336", {"start": v(-175, -55.15) * mm, "end": v(-175, -58.15) * mm});
            skLineSegment(sketch, "E337", {"start": v(-175, -58.15) * mm, "end": v(-176, -58.15) * mm});
            skArc(sketch, "E338", {"start": v(-176, -58.15) * mm, "mid": v(-176.7, -58.45) * mm, "end": v(-177, -59.15) * mm});
            skLineSegment(sketch, "E339", {"start": v(-177, -59.15) * mm, "end": v(-177, -92.15) * mm});
            skArc(sketch, "E340", {"start": v(-177, -92.15) * mm, "mid": v(-176.7, -92.86) * mm, "end": v(-176, -93.15) * mm});
            skLineSegment(sketch, "E341", {"start": v(-176, -93.15) * mm, "end": v(-175, -93.15) * mm});
            skLineSegment(sketch, "E342", {"start": v(-175, -93.15) * mm, "end": v(-175, -96.15) * mm});
            skLineSegment(sketch, "E343", {"start": v(-175, -96.15) * mm, "end": v(-176, -96.15) * mm});
            skArc(sketch, "E344", {"start": v(-176, -96.15) * mm, "mid": v(-176.7, -96.45) * mm, "end": v(-177, -97.15) * mm});
            skLineSegment(sketch, "E345", {"start": v(-177, -97.15) * mm, "end": v(-177, -141.69) * mm});
            skArc(sketch, "E346", {"start": v(-177, -141.69) * mm, "mid": v(-176.93, -141.94) * mm, "end": v(-176.75, -142.12) * mm});
            skArc(sketch, "E347", {"start": v(-177.43, -142.8) * mm, "mid": v(-176.65, -142.9) * mm, "end": v(-176.75, -142.12) * mm});
            skArc(sketch, "E348", {"start": v(-177.43, -142.8) * mm, "mid": v(-177.62, -142.62) * mm, "end": v(-177.87, -142.55) * mm});
            skLineSegment(sketch, "E349", {"start": v(-177.87, -142.55) * mm, "end": v(-179.5, -142.55) * mm});
            skArc(sketch, "E350", {"start": v(-179.5, -142.55) * mm, "mid": v(-179.85, -142.7) * mm, "end": v(-180, -143.05) * mm});
            skLineSegment(sketch, "E351", {"start": v(-180, -143.05) * mm, "end": v(-180, -148.05) * mm});
            skArc(sketch, "E352", {"start": v(-180, -148.05) * mm, "mid": v(-179.85, -148.4) * mm, "end": v(-179.5, -148.55) * mm});
            skLineSegment(sketch, "E353", {"start": v(-179.5, -148.55) * mm, "end": v(-177.87, -148.55) * mm});
            skArc(sketch, "E354", {"start": v(-177.87, -148.55) * mm, "mid": v(-177.62, -148.49) * mm, "end": v(-177.43, -148.3) * mm});
            skArc(sketch, "E355", {"start": v(-176.75, -148.99) * mm, "mid": v(-176.65, -148.2) * mm, "end": v(-177.43, -148.3) * mm});
            skArc(sketch, "E356", {"start": v(-176.75, -148.99) * mm, "mid": v(-176.93, -149.17) * mm, "end": v(-177, -149.42) * mm});
            skLineSegment(sketch, "E357", {"start": v(-177, -149.42) * mm, "end": v(-177, -154.55) * mm});
            skLineSegment(sketch, "E358", {"start": v(-177, -154.55) * mm, "end": v(-174, -154.55) * mm});
            skLineSegment(sketch, "E359", {"start": v(-174, -154.55) * mm, "end": v(-174, -153.28) * mm});
            skLineSegment(sketch, "E360", {"start": v(-174, -153.28) * mm, "end": v(-170, -153.28) * mm});
            skLineSegment(sketch, "E361", {"start": v(-170, -153.28) * mm, "end": v(-170, -154.55) * mm});
            skLineSegment(sketch, "E362", {"start": v(-170, -154.55) * mm, "end": v(-167, -154.55) * mm});
            skLineSegment(sketch, "E363", {"start": v(-167, -154.55) * mm, "end": v(-167, -157.75) * mm});
            skLineSegment(sketch, "E364", {"start": v(-167, -157.75) * mm, "end": v(-170, -157.75) * mm});
            skLineSegment(sketch, "E365", {"start": v(-170, -157.75) * mm, "end": v(-170, -159.03) * mm});
            skLineSegment(sketch, "E366", {"start": v(-170, -159.03) * mm, "end": v(-174, -159.03) * mm});
            skLineSegment(sketch, "E367", {"start": v(-174, -159.03) * mm, "end": v(-174, -157.75) * mm});
            skLineSegment(sketch, "E368", {"start": v(-174, -157.75) * mm, "end": v(-177, -157.75) * mm});
            skLineSegment(sketch, "E369", {"start": v(-177, -157.75) * mm, "end": v(-177, -162.89) * mm});
            skArc(sketch, "E370", {"start": v(-177, -162.89) * mm, "mid": v(-176.93, -163.14) * mm, "end": v(-176.75, -163.32) * mm});
            skArc(sketch, "E371", {"start": v(-177.43, -164) * mm, "mid": v(-176.65, -164.1) * mm, "end": v(-176.75, -163.32) * mm});
            skArc(sketch, "E372", {"start": v(-177.43, -164) * mm, "mid": v(-177.62, -163.82) * mm, "end": v(-177.87, -163.75) * mm});
            skLineSegment(sketch, "E373", {"start": v(-177.87, -163.75) * mm, "end": v(-179.5, -163.75) * mm});
            skArc(sketch, "E374", {"start": v(-179.5, -163.75) * mm, "mid": v(-179.85, -163.9) * mm, "end": v(-180, -164.25) * mm});
            skLineSegment(sketch, "E375", {"start": v(-180, -164.25) * mm, "end": v(-180, -169.25) * mm});
            skArc(sketch, "E376", {"start": v(-180, -169.25) * mm, "mid": v(-179.85, -169.6) * mm, "end": v(-179.5, -169.75) * mm});
            skLineSegment(sketch, "E377", {"start": v(-179.5, -169.75) * mm, "end": v(-177.87, -169.75) * mm});
            skArc(sketch, "E378", {"start": v(-177.87, -169.75) * mm, "mid": v(-177.62, -169.69) * mm, "end": v(-177.43, -169.5) * mm});
            skArc(sketch, "E379", {"start": v(-176.75, -170.19) * mm, "mid": v(-176.65, -169.4) * mm, "end": v(-177.43, -169.5) * mm});
            skArc(sketch, "E380", {"start": v(-176.75, -170.19) * mm, "mid": v(-176.93, -170.37) * mm, "end": v(-177, -170.62) * mm});
            skLineSegment(sketch, "E381", {"start": v(-177, -170.62) * mm, "end": v(-177, -181.15) * mm});
            skLineSegment(sketch, "E382", {"start": v(-177, -181.15) * mm, "end": v(-156.83, -181.15) * mm});
            skArc(sketch, "E383", {"start": v(-156.83, -181.15) * mm, "mid": v(-156.06, -181) * mm, "end": v(-155.41, -180.57) * mm});
            skLineSegment(sketch, "E384", {"start": v(-155.41, -180.57) * mm, "end": v(-154.59, -179.74) * mm});
            skArc(sketch, "E385", {"start": v(-153.17, -179.15) * mm, "mid": v(-153.94, -179.3) * mm, "end": v(-154.59, -179.74) * mm});
            skLineSegment(sketch, "E386", {"start": v(-153.17, -179.15) * mm, "end": v(-47, -179.15) * mm});
            skLineSegment(sketch, "E387", {"start": v(-47, -179.15) * mm, "end": v(-47, -170.62) * mm});
            skLineSegment(sketch, "E388", {"start": v(-62, -165.15) * mm, "end": v(-110, -165.15) * mm});
            skArc(sketch, "E389", {"start": v(-62, -173.15) * mm, "mid": v(-58, -169.15) * mm, "end": v(-62, -165.15) * mm});
            skLineSegment(sketch, "E390", {"start": v(-110, -173.15) * mm, "end": v(-62, -173.15) * mm});
            skArc(sketch, "E391", {"start": v(-110, -165.15) * mm, "mid": v(-114, -169.15) * mm, "end": v(-110, -173.15) * mm});
            skArc(sketch, "E392", {"start": v(24.37, -157.8) * mm, "mid": v(24.12, -157.87) * mm, "end": v(23.93, -158.05) * mm});
            skArc(sketch, "E393", {"start": v(23.25, -157.37) * mm, "mid": v(23.15, -158.16) * mm, "end": v(23.93, -158.05) * mm});
            skArc(sketch, "E394", {"start": v(23.25, -157.37) * mm, "mid": v(23.43, -157.19) * mm, "end": v(23.5, -156.94) * mm});
            skLineSegment(sketch, "E395", {"start": v(23.5, -155.37) * mm, "end": v(23.5, -156.94) * mm});
            skArc(sketch, "E396", {"start": v(23.5, -155.37) * mm, "mid": v(23.43, -155.12) * mm, "end": v(23.25, -154.94) * mm});
            skArc(sketch, "E397", {"start": v(23.93, -154.25) * mm, "mid": v(23.15, -154.15) * mm, "end": v(23.25, -154.94) * mm});
            skArc(sketch, "E398", {"start": v(23.93, -154.25) * mm, "mid": v(24.12, -154.44) * mm, "end": v(24.37, -154.5) * mm});
            skLineSegment(sketch, "E399", {"start": v(28.83, -154.5) * mm, "end": v(24.37, -154.5) * mm});
            skArc(sketch, "E400", {"start": v(28.83, -154.5) * mm, "mid": v(29.08, -154.44) * mm, "end": v(29.27, -154.25) * mm});
            skArc(sketch, "E401", {"start": v(29.95, -154.94) * mm, "mid": v(30.05, -154.15) * mm, "end": v(29.27, -154.25) * mm});
            skArc(sketch, "E402", {"start": v(29.95, -154.94) * mm, "mid": v(29.77, -155.12) * mm, "end": v(29.7, -155.37) * mm});
            skLineSegment(sketch, "E403", {"start": v(29.7, -156.94) * mm, "end": v(29.7, -155.37) * mm});
            skArc(sketch, "E404", {"start": v(29.7, -156.94) * mm, "mid": v(29.77, -157.19) * mm, "end": v(29.95, -157.37) * mm});
            skArc(sketch, "E405", {"start": v(29.27, -158.05) * mm, "mid": v(30.05, -158.16) * mm, "end": v(29.95, -157.37) * mm});
            skArc(sketch, "E406", {"start": v(29.27, -158.05) * mm, "mid": v(29.08, -157.87) * mm, "end": v(28.83, -157.8) * mm});
            skLineSegment(sketch, "E407", {"start": v(24.37, -157.8) * mm, "end": v(28.83, -157.8) * mm});
            skArc(sketch, "E408", {"start": v(3.17, -157.8) * mm, "mid": v(2.92, -157.87) * mm, "end": v(2.73, -158.05) * mm});
            skArc(sketch, "E409", {"start": v(2.05, -157.37) * mm, "mid": v(1.95, -158.16) * mm, "end": v(2.73, -158.05) * mm});
            skArc(sketch, "E410", {"start": v(2.05, -157.37) * mm, "mid": v(2.23, -157.19) * mm, "end": v(2.3, -156.94) * mm});
            skLineSegment(sketch, "E411", {"start": v(2.3, -155.37) * mm, "end": v(2.3, -156.94) * mm});
            skArc(sketch, "E412", {"start": v(2.3, -155.37) * mm, "mid": v(2.23, -155.12) * mm, "end": v(2.05, -154.94) * mm});
            skArc(sketch, "E413", {"start": v(2.73, -154.25) * mm, "mid": v(1.95, -154.15) * mm, "end": v(2.05, -154.94) * mm});
            skArc(sketch, "E414", {"start": v(2.73, -154.25) * mm, "mid": v(2.92, -154.44) * mm, "end": v(3.17, -154.5) * mm});
            skLineSegment(sketch, "E415", {"start": v(7.63, -154.5) * mm, "end": v(3.17, -154.5) * mm});
            skArc(sketch, "E416", {"start": v(7.63, -154.5) * mm, "mid": v(7.88, -154.44) * mm, "end": v(8.07, -154.25) * mm});
            skArc(sketch, "E417", {"start": v(8.75, -154.94) * mm, "mid": v(8.85, -154.15) * mm, "end": v(8.07, -154.25) * mm});
            skArc(sketch, "E418", {"start": v(8.75, -154.94) * mm, "mid": v(8.57, -155.12) * mm, "end": v(8.5, -155.37) * mm});
            skLineSegment(sketch, "E419", {"start": v(8.5, -156.94) * mm, "end": v(8.5, -155.37) * mm});
            skArc(sketch, "E420", {"start": v(8.5, -156.94) * mm, "mid": v(8.57, -157.19) * mm, "end": v(8.75, -157.37) * mm});
            skArc(sketch, "E421", {"start": v(8.07, -158.05) * mm, "mid": v(8.85, -158.16) * mm, "end": v(8.75, -157.37) * mm});
            skArc(sketch, "E422", {"start": v(8.07, -158.05) * mm, "mid": v(7.88, -157.87) * mm, "end": v(7.63, -157.8) * mm});
            skLineSegment(sketch, "E423", {"start": v(3.17, -157.8) * mm, "end": v(7.63, -157.8) * mm});
            skCircle(sketch, "E424", {"center": v(-162, 141.35) * mm, "radius": 1.55 * mm});
            skLineSegment(sketch, "E425", {"start": v(-78, 147.85) * mm, "end": v(-58, 147.85) * mm});
            skArc(sketch, "E426", {"start": v(-78, 155.85) * mm, "mid": v(-82, 151.85) * mm, "end": v(-78, 147.85) * mm});
            skLineSegment(sketch, "E427", {"start": v(-58, 155.85) * mm, "end": v(-78, 155.85) * mm});
            skArc(sketch, "E428", {"start": v(-58, 147.85) * mm, "mid": v(-54, 151.85) * mm, "end": v(-58, 155.85) * mm});
            skCircle(sketch, "E429", {"center": v(-117, -156.15) * mm, "radius": 1.6 * mm});
            skArc(sketch, "E430", {"start": v(-143.63, -142.8) * mm, "mid": v(-143.88, -142.87) * mm, "end": v(-144.07, -143.05) * mm});
            skArc(sketch, "E431", {"start": v(-144.75, -142.37) * mm, "mid": v(-144.85, -143.16) * mm, "end": v(-144.07, -143.05) * mm});
            skArc(sketch, "E432", {"start": v(-144.75, -142.37) * mm, "mid": v(-144.57, -142.19) * mm, "end": v(-144.5, -141.94) * mm});
            skLineSegment(sketch, "E433", {"start": v(-144.5, -140.37) * mm, "end": v(-144.5, -141.94) * mm});
            skArc(sketch, "E434", {"start": v(-144.5, -140.37) * mm, "mid": v(-144.57, -140.12) * mm, "end": v(-144.75, -139.94) * mm});
            skArc(sketch, "E435", {"start": v(-144.07, -139.25) * mm, "mid": v(-144.85, -139.15) * mm, "end": v(-144.75, -139.94) * mm});
            skArc(sketch, "E436", {"start": v(-144.07, -139.25) * mm, "mid": v(-143.88, -139.44) * mm, "end": v(-143.63, -139.5) * mm});
            skLineSegment(sketch, "E437", {"start": v(-139.17, -139.5) * mm, "end": v(-143.63, -139.5) * mm});
            skArc(sketch, "E438", {"start": v(-139.17, -139.5) * mm, "mid": v(-138.92, -139.44) * mm, "end": v(-138.73, -139.25) * mm});
            skArc(sketch, "E439", {"start": v(-138.05, -139.94) * mm, "mid": v(-137.95, -139.15) * mm, "end": v(-138.73, -139.25) * mm});
            skArc(sketch, "E440", {"start": v(-138.05, -139.94) * mm, "mid": v(-138.23, -140.12) * mm, "end": v(-138.3, -140.37) * mm});
            skLineSegment(sketch, "E441", {"start": v(-138.3, -141.94) * mm, "end": v(-138.3, -140.37) * mm});
            skArc(sketch, "E442", {"start": v(-138.3, -141.94) * mm, "mid": v(-138.23, -142.19) * mm, "end": v(-138.05, -142.37) * mm});
            skArc(sketch, "E443", {"start": v(-138.73, -143.05) * mm, "mid": v(-137.95, -143.16) * mm, "end": v(-138.05, -142.37) * mm});
            skArc(sketch, "E444", {"start": v(-138.73, -143.05) * mm, "mid": v(-138.92, -142.87) * mm, "end": v(-139.17, -142.8) * mm});
            skLineSegment(sketch, "E445", {"start": v(-143.63, -142.8) * mm, "end": v(-139.17, -142.8) * mm});
            skArc(sketch, "E446", {"start": v(-164.83, -142.8) * mm, "mid": v(-165.08, -142.87) * mm, "end": v(-165.27, -143.05) * mm});
            skArc(sketch, "E447", {"start": v(-165.95, -142.37) * mm, "mid": v(-166.05, -143.16) * mm, "end": v(-165.27, -143.05) * mm});
            skArc(sketch, "E448", {"start": v(-165.95, -142.37) * mm, "mid": v(-165.77, -142.19) * mm, "end": v(-165.7, -141.94) * mm});
            skLineSegment(sketch, "E449", {"start": v(-165.7, -140.37) * mm, "end": v(-165.7, -141.94) * mm});
            skArc(sketch, "E450", {"start": v(-165.7, -140.37) * mm, "mid": v(-165.77, -140.12) * mm, "end": v(-165.95, -139.94) * mm});
            skArc(sketch, "E451", {"start": v(-165.27, -139.25) * mm, "mid": v(-166.05, -139.15) * mm, "end": v(-165.95, -139.94) * mm});
            skArc(sketch, "E452", {"start": v(-165.27, -139.25) * mm, "mid": v(-165.08, -139.44) * mm, "end": v(-164.83, -139.5) * mm});
            skLineSegment(sketch, "E453", {"start": v(-160.37, -139.5) * mm, "end": v(-164.83, -139.5) * mm});
            skArc(sketch, "E454", {"start": v(-160.37, -139.5) * mm, "mid": v(-160.12, -139.44) * mm, "end": v(-159.93, -139.25) * mm});
            skArc(sketch, "E455", {"start": v(-159.25, -139.94) * mm, "mid": v(-159.15, -139.15) * mm, "end": v(-159.93, -139.25) * mm});
            skArc(sketch, "E456", {"start": v(-159.25, -139.94) * mm, "mid": v(-159.43, -140.12) * mm, "end": v(-159.5, -140.37) * mm});
            skLineSegment(sketch, "E457", {"start": v(-159.5, -141.94) * mm, "end": v(-159.5, -140.37) * mm});
            skArc(sketch, "E458", {"start": v(-159.5, -141.94) * mm, "mid": v(-159.43, -142.19) * mm, "end": v(-159.25, -142.37) * mm});
            skArc(sketch, "E459", {"start": v(-159.93, -143.05) * mm, "mid": v(-159.15, -143.16) * mm, "end": v(-159.25, -142.37) * mm});
            skArc(sketch, "E460", {"start": v(-159.93, -143.05) * mm, "mid": v(-160.12, -142.87) * mm, "end": v(-160.37, -142.8) * mm});
            skLineSegment(sketch, "E461", {"start": v(-164.83, -142.8) * mm, "end": v(-160.37, -142.8) * mm});
            skCircle(sketch, "E462", {"center": v(-57, 29.35) * mm, "radius": 1.55 * mm});
            skCircle(sketch, "E463", {"center": v(-57, -94.65) * mm, "radius": 1.55 * mm});
            skCircle(sketch, "E464", {"center": v(-57, 84.35) * mm, "radius": 1.55 * mm});
            skCircle(sketch, "E465", {"center": v(-67, -56.65) * mm, "radius": 1.6 * mm});
            skCircle(sketch, "E466", {"center": v(-67, 84.35) * mm, "radius": 1.55 * mm});
            skCircle(sketch, "E467", {"center": v(-67, 141.35) * mm, "radius": 1.55 * mm});
            skLineSegment(sketch, "E468", {"start": v(-130.87, -56.1) * mm, "end": v(-130.87, -49.74) * mm});
            skArc(sketch, "E469", {"start": v(-134.07, -56.1) * mm, "mid": v(-132.47, -57.7) * mm, "end": v(-130.87, -56.1) * mm});
            skLineSegment(sketch, "E470", {"start": v(-134.07, -49.74) * mm, "end": v(-134.07, -56.1) * mm});
            skArc(sketch, "E471", {"start": v(-130.87, -49.74) * mm, "mid": v(-132.47, -48.14) * mm, "end": v(-134.07, -49.74) * mm});
            skLineSegment(sketch, "E472", {"start": v(-82.6, 25.19) * mm, "end": v(-82.6, 31.54) * mm});
            skArc(sketch, "E473", {"start": v(-85.8, 25.19) * mm, "mid": v(-84.2, 23.59) * mm, "end": v(-82.6, 25.19) * mm});
            skLineSegment(sketch, "E474", {"start": v(-85.8, 31.54) * mm, "end": v(-85.8, 25.19) * mm});
            skArc(sketch, "E475", {"start": v(-82.6, 31.54) * mm, "mid": v(-84.2, 33.14) * mm, "end": v(-85.8, 31.54) * mm});
            skLineSegment(sketch, "E476", {"start": v(-82.6, -51.01) * mm, "end": v(-82.6, -49.74) * mm});
            skArc(sketch, "E477", {"start": v(-85.8, -51.01) * mm, "mid": v(-84.2, -52.61) * mm, "end": v(-82.6, -51.01) * mm});
            skLineSegment(sketch, "E478", {"start": v(-85.8, -49.74) * mm, "end": v(-85.8, -51.01) * mm});
            skArc(sketch, "E479", {"start": v(-82.6, -49.74) * mm, "mid": v(-84.2, -48.14) * mm, "end": v(-85.8, -49.74) * mm});
            skCircle(sketch, "E480", {"center": v(-89.29, 1.06) * mm, "radius": 1.6 * mm});
            skCircle(sketch, "E481", {"center": v(-138.14, 6.43) * mm, "radius": 1.6 * mm});
            skCircle(sketch, "E482", {"center": v(-68.2, -87.77) * mm, "radius": 2.1 * mm});
            skLineSegment(sketch, "E483", {"start": v(-146.5, 48.03) * mm, "end": v(-146.5, 46.03) * mm});
            skArc(sketch, "E484", {"start": v(-142.3, 48.03) * mm, "mid": v(-144.4, 50.13) * mm, "end": v(-146.5, 48.03) * mm});
            skLineSegment(sketch, "E485", {"start": v(-142.3, 46.03) * mm, "end": v(-142.3, 48.03) * mm});
            skArc(sketch, "E486", {"start": v(-146.5, 46.03) * mm, "mid": v(-144.4, 43.93) * mm, "end": v(-142.3, 46.03) * mm});
            skLineSegment(sketch, "E487", {"start": v(-70.3, 48.03) * mm, "end": v(-70.3, 46.03) * mm});
            skArc(sketch, "E488", {"start": v(-66.1, 48.03) * mm, "mid": v(-68.2, 50.13) * mm, "end": v(-70.3, 48.03) * mm});
            skLineSegment(sketch, "E489", {"start": v(-66.1, 46.03) * mm, "end": v(-66.1, 48.03) * mm});
            skArc(sketch, "E490", {"start": v(-70.3, 46.03) * mm, "mid": v(-68.2, 43.93) * mm, "end": v(-66.1, 46.03) * mm});
            skCircle(sketch, "E491", {"center": v(-96.63, -48.24) * mm, "radius": 1.6 * mm});
            skCircle(sketch, "E492", {"center": v(-147.73, -81.44) * mm, "radius": 1.6 * mm});
            skCircle(sketch, "E493", {"center": v(-117.23, 1.06) * mm, "radius": 1.6 * mm});
            skCircle(sketch, "E494", {"center": v(-89.03, -81.44) * mm, "radius": 1.6 * mm});
            skCircle(sketch, "E495", {"center": v(-158.5, -102.65) * mm, "radius": 1.6 * mm});
            skCircle(sketch, "E496", {"center": v(-158.5, 40.35) * mm, "radius": 1.6 * mm});
            skCircle(sketch, "E497", {"center": v(-144.4, -87.77) * mm, "radius": 2.1 * mm});
            skLineSegment(sketch, "E498", {"start": v(-138.14, -93.57) * mm, "end": v(-140.88, -93.57) * mm});
            skArc(sketch, "E499", {"start": v(-138.14, -96.77) * mm, "mid": v(-136.54, -95.17) * mm, "end": v(-138.14, -93.57) * mm});
            skLineSegment(sketch, "E500", {"start": v(-140.88, -96.77) * mm, "end": v(-138.14, -96.77) * mm});
            skArc(sketch, "E501", {"start": v(-140.88, -93.57) * mm, "mid": v(-142.48, -95.17) * mm, "end": v(-140.88, -96.77) * mm});
            skCircle(sketch, "E502", {"center": v(-104.88, -95.17) * mm, "radius": 1.6 * mm});
            skCircle(sketch, "E503", {"center": v(-162, -18.65) * mm, "radius": 1.55 * mm});
            skCircle(sketch, "E504", {"center": v(-162, -94.65) * mm, "radius": 1.6 * mm});
            skCircle(sketch, "E505", {"center": v(-147, -121.15) * mm, "radius": 1.6 * mm});
            skCircle(sketch, "E506", {"center": v(-107, -121.15) * mm, "radius": 1.6 * mm});
            skCircle(sketch, "E507", {"center": v(-67, -121.15) * mm, "radius": 1.6 * mm});
            skCircle(sketch, "E508", {"center": v(-135.4, -71.15) * mm, "radius": 2.23 * mm});
            skCircle(sketch, "E509", {"center": v(-132.08, -5.05) * mm, "radius": 2.23 * mm});
            skCircle(sketch, "E510", {"center": v(-151.88, 52.83) * mm, "radius": 1.6 * mm});
            skCircle(sketch, "E511", {"center": v(-73.88, -95.17) * mm, "radius": 1.6 * mm});
            skLineSegment(sketch, "E512", {"start": v(-157, 126.47) * mm, "end": v(-137, 126.47) * mm});
            skArc(sketch, "E513", {"start": v(-157, 129.22) * mm, "mid": v(-158.38, 127.85) * mm, "end": v(-157, 126.47) * mm});
            skLineSegment(sketch, "E514", {"start": v(-137, 129.22) * mm, "end": v(-157, 129.22) * mm});
            skArc(sketch, "E515", {"start": v(-137, 126.47) * mm, "mid": v(-135.63, 127.85) * mm, "end": v(-137, 129.22) * mm});
            skLineSegment(sketch, "E516", {"start": v(-157, 77.47) * mm, "end": v(-137, 77.47) * mm});
            skArc(sketch, "E517", {"start": v(-157, 80.22) * mm, "mid": v(-158.38, 78.85) * mm, "end": v(-157, 77.47) * mm});
            skLineSegment(sketch, "E518", {"start": v(-137, 80.22) * mm, "end": v(-157, 80.22) * mm});
            skArc(sketch, "E519", {"start": v(-137, 77.47) * mm, "mid": v(-135.63, 78.85) * mm, "end": v(-137, 80.22) * mm});
            skLineSegment(sketch, "E520", {"start": v(-99, 126.47) * mm, "end": v(-79, 126.47) * mm});
            skArc(sketch, "E521", {"start": v(-99, 129.22) * mm, "mid": v(-100.38, 127.85) * mm, "end": v(-99, 126.47) * mm});
            skLineSegment(sketch, "E522", {"start": v(-79, 129.22) * mm, "end": v(-99, 129.22) * mm});
            skArc(sketch, "E523", {"start": v(-79, 126.47) * mm, "mid": v(-77.63, 127.85) * mm, "end": v(-79, 129.22) * mm});
            skLineSegment(sketch, "E524", {"start": v(-99, 77.47) * mm, "end": v(-79, 77.47) * mm});
            skArc(sketch, "E525", {"start": v(-99, 80.22) * mm, "mid": v(-100.38, 78.85) * mm, "end": v(-99, 77.47) * mm});
            skLineSegment(sketch, "E526", {"start": v(-79, 80.22) * mm, "end": v(-99, 80.22) * mm});
            skArc(sketch, "E527", {"start": v(-79, 77.47) * mm, "mid": v(-77.63, 78.85) * mm, "end": v(-79, 80.22) * mm});
            skLineSegment(sketch, "E528", {"start": v(-157, 116.47) * mm, "end": v(-137, 116.47) * mm});
            skArc(sketch, "E529", {"start": v(-157, 119.22) * mm, "mid": v(-158.38, 117.85) * mm, "end": v(-157, 116.47) * mm});
            skLineSegment(sketch, "E530", {"start": v(-137, 119.22) * mm, "end": v(-157, 119.22) * mm});
            skArc(sketch, "E531", {"start": v(-137, 116.47) * mm, "mid": v(-135.63, 117.85) * mm, "end": v(-137, 119.22) * mm});
            skLineSegment(sketch, "E532", {"start": v(-157, 67.47) * mm, "end": v(-137, 67.47) * mm});
            skArc(sketch, "E533", {"start": v(-157, 70.22) * mm, "mid": v(-158.38, 68.85) * mm, "end": v(-157, 67.47) * mm});
            skLineSegment(sketch, "E534", {"start": v(-137, 70.22) * mm, "end": v(-157, 70.22) * mm});
            skArc(sketch, "E535", {"start": v(-137, 67.47) * mm, "mid": v(-135.63, 68.85) * mm, "end": v(-137, 70.22) * mm});
            skLineSegment(sketch, "E536", {"start": v(-99, 116.47) * mm, "end": v(-79, 116.47) * mm});
            skArc(sketch, "E537", {"start": v(-99, 119.22) * mm, "mid": v(-100.38, 117.85) * mm, "end": v(-99, 116.47) * mm});
            skLineSegment(sketch, "E538", {"start": v(-79, 119.22) * mm, "end": v(-99, 119.22) * mm});
            skArc(sketch, "E539", {"start": v(-79, 116.47) * mm, "mid": v(-77.63, 117.85) * mm, "end": v(-79, 119.22) * mm});
            skLineSegment(sketch, "E540", {"start": v(-99, 67.47) * mm, "end": v(-79, 67.47) * mm});
            skArc(sketch, "E541", {"start": v(-99, 70.22) * mm, "mid": v(-100.38, 68.85) * mm, "end": v(-99, 67.47) * mm});
            skLineSegment(sketch, "E542", {"start": v(-79, 70.22) * mm, "end": v(-99, 70.22) * mm});
            skArc(sketch, "E543", {"start": v(-79, 67.47) * mm, "mid": v(-77.63, 68.85) * mm, "end": v(-79, 70.22) * mm});
            skCircle(sketch, "E544", {"center": v(-77, 141.35) * mm, "radius": 1.55 * mm});
            skCircle(sketch, "E545", {"center": v(117, -156.15) * mm, "radius": 1.6 * mm});
            skCircle(sketch, "E546", {"center": v(29.25, -165.45) * mm, "radius": 1.55 * mm});
            skCircle(sketch, "E547", {"center": v(103.25, -165.45) * mm, "radius": 1.55 * mm});
            skCircle(sketch, "E548", {"center": v(29.25, -146.86) * mm, "radius": 1.55 * mm});
            skCircle(sketch, "E549", {"center": v(163.25, -146.86) * mm, "radius": 1.55 * mm});
            skSolve(sketch);
        }
        {
            var Q0;
            Q0 = qSketchRegion(id + "F0", true);
            extrude(context, id + "F1", {"entities" : qUnion([Q0]), "depth" : 3 * mm, "offsetDistance" : 25 * mm});
        }
    });
